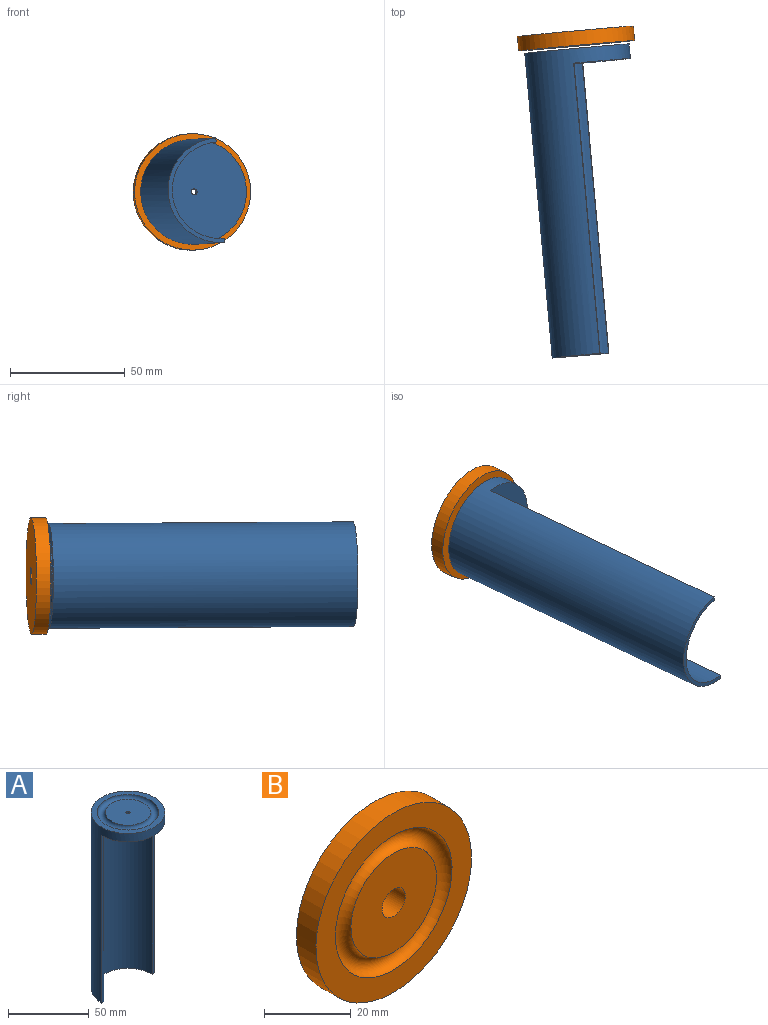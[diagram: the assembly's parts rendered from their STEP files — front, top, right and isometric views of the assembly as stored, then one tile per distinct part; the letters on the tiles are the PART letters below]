
ASSEMBLY  parts=2 mates=1
PART A: 10 faces, bbox 45.7x45.7x135.2 mm
  f0: plane 45.72x43.94mm, normal (0,0,-1), area 1513.9mm2, adj f2,f3,f6,f7,f8
  f1: plane 27.94x27.94mm, normal (0,0,1), area 608mm2, adj f2,f5
  f2: cylinder r=1.27mm len=6.35mm, axis (0,0,-1), area 50.7mm2, adj f0,f1
  f3: cylinder r=22.86mm len=133.35mm, axis (0,0,-1), area 10032.8mm2, adj f0,f4,f7,f8,f9
  f4: plane 45.72x45.72mm, normal (0,0,1), area 501.6mm2, adj f3,f5
  f5: torus R=16.51mm, axis (0,0,1), area 827.8mm2, adj f1,f4
  f6: cylinder r=21.08mm len=127mm, axis (0,0,1), area 8411.3mm2, adj f0,f7,f8,f9
  f7: plane 127x1.78mm, normal (0,-1,0), area 225.8mm2, adj f0,f3,f6,f9
  f8: plane 127x1.78mm, normal (0,-1,0), area 225.8mm2, adj f0,f3,f6,f9
  f9: plane 45.72x22.86mm, normal (0,0,-1), area 122.7mm2, adj f3,f6,f7,f8
PART B: 6 faces, bbox 50.8x8.2x50.8 mm
  f0: plane 27.94x27.94mm, normal (0,-1,0), area 567.5mm2, adj f1,f5
  f1: cylinder r=3.81mm len=7.62mm, axis (0,1,0), area 152mm2, adj f0,f4
  f2: cylinder r=25.4mm len=50.8mm, axis (0,1,0), area 1013.4mm2, adj f3,f4
  f3: plane 50.8x50.8mm, normal (0,-1,0), area 886.7mm2, adj f2,f5
  f4: plane 50.8x50.8mm, normal (0,1,0), area 1981.2mm2, adj f1,f2
  f5: torus R=16.51mm, axis (0,-1,0), area 827.8mm2, adj f0,f3
PLACE A rot(axis=(-0.63,0.52,0.58),120.3deg) t=(-15.56,-28.41,-4.95)mm
PLACE B rot(axis=(-0.05,1,0.05),85.1deg) t=(-16.81,-14.5,-5.04)mm
MATE parallel A.f3 <-> B.f2  axis (-0.09,1,-0.01) through (-16.13,-22.09,-4.99)mm
